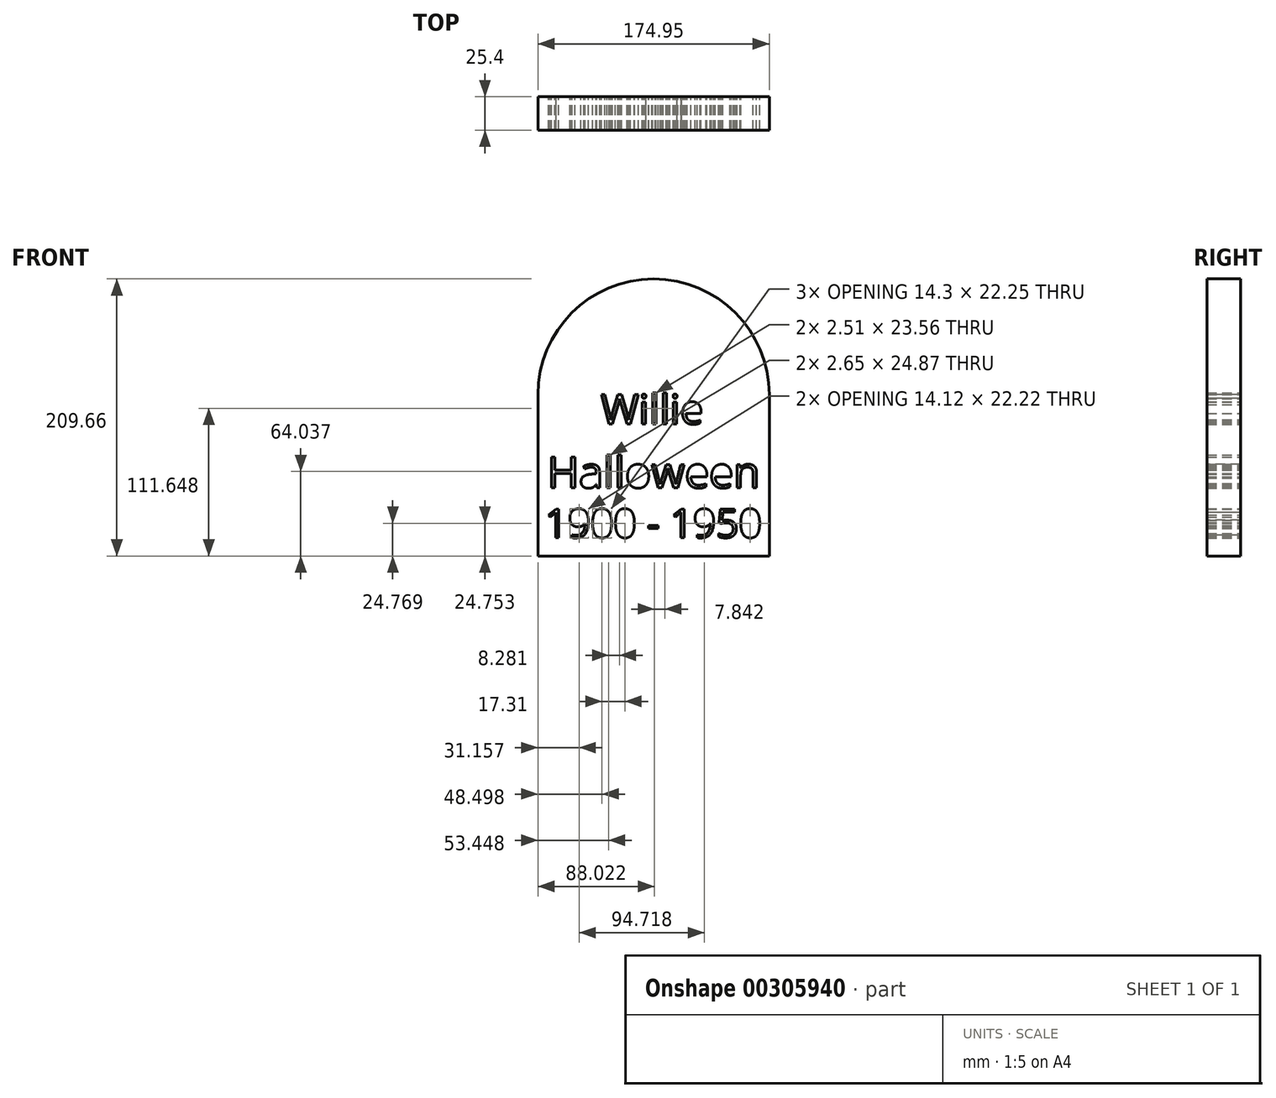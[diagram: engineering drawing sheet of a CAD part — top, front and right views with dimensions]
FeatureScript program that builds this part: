
annotation { "Feature Type Name" : "Feature", "Feature Type Description" : "" }
export const myFeature = defineFeature(function(context is Context, id is Id, definition is map)
    precondition{}
    {
        {
            var Q0;
            Q0=qCreatedBy(makeId("Front.planeOp"),FACE);
            var sketch = newSketch(context, id + "F0", { "sketchPlane" : qUnion([Q0])});
            skLineSegment(sketch, "E0", {"start": v(-86.88, 47.02) * mm, "end": v(-86.88, -75.17) * mm});
            skLineSegment(sketch, "E1", {"start": v(88.07, 47.02) * mm, "end": v(88.07, -75.17) * mm});
            skArc(sketch, "E2", {"start": v(88.07, 47.02) * mm, "mid": v(0.6, 134.5) * mm, "end": v(-86.88, 47.02) * mm});
            skLineSegment(sketch, "E3", {"start": v(-86.88, -75.17) * mm, "end": v(88.07, -75.17) * mm});
            skText(sketch, "E4", { "text": "Willie", "fontName": "OpenSans-Regular.ttf"});
            skText(sketch, "E5", { "text": "Halloween", "fontName": "OpenSans-Regular.ttf"});
            skText(sketch, "E6", { "text": "1900 - 1950", "fontName": "OpenSans-Regular.ttf"});
            const initialGuessF0  = {"E4": [-0.03932, 0.0247, 1, 0, 0.02232], "E5": [-0.07993, -0.02357, 1, 0, 0.02357], "E6": [-0.08166, -0.06123, 1, 0, 0.0218]};
            skSetInitialGuess(sketch, initialGuessF0);
            skSolve(sketch);
        }
        {
            var Q0;
            Q0=makeQuery(id+"F0.imprint","IMPRINT",FACE,{"disambiguationData":[TD([[makeQuery(id+"F0.imprint","IMPRINT",EDGE,{"derivedFrom":sQuery(id+"F0.wireOp",EDGE,"E0")}),1.0]])]});
            extrude(context, id + "F1", {"entities" : qUnion([Q0]), "depth" : 25.4 * mm});
        }
    });
